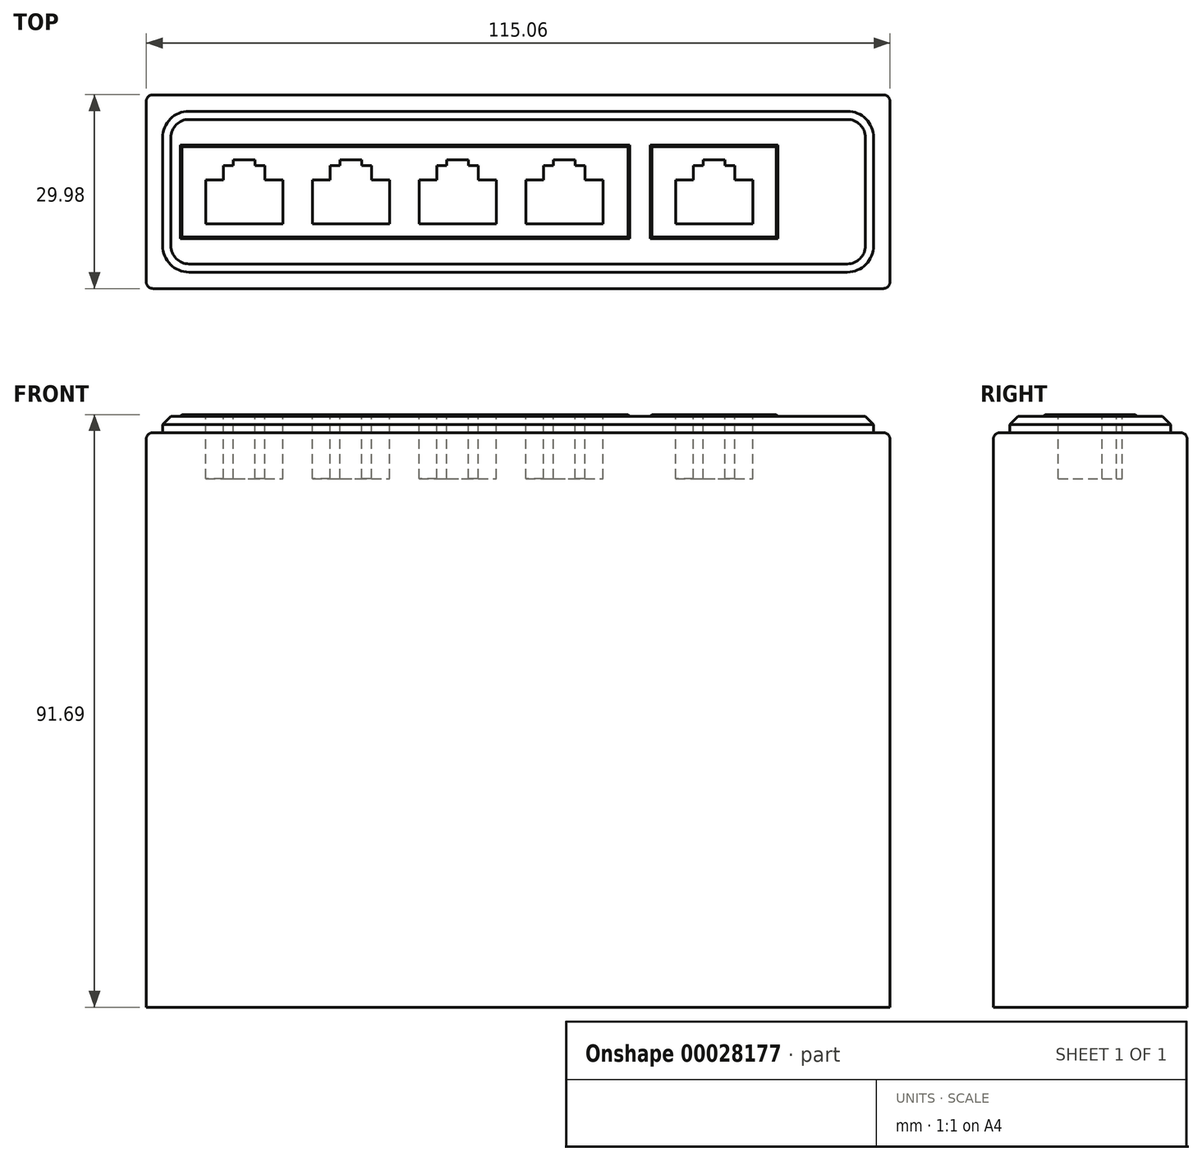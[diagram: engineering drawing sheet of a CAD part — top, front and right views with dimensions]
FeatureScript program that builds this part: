
annotation { "Feature Type Name" : "Feature", "Feature Type Description" : "" }
export const myFeature = defineFeature(function(context is Context, id is Id, definition is map)
    precondition{}
    {
        {
            var Q0;
            Q0=qCreatedBy(makeId("Front.planeOp"),FACE);
            var sketch = newSketch(context, id + "F0", { "sketchPlane" : qUnion([Q0])});
            skLineSegment(sketch, "E0.bottom", {"start": v(-57.53, -45.72) * mm, "end": v(57.53, -45.72) * mm});
            skLineSegment(sketch, "E0.top", {"start": v(-57.53, 43.18) * mm, "end": v(57.53, 43.18) * mm});
            skLineSegment(sketch, "E0.left", {"start": v(-57.53, -45.72) * mm, "end": v(-57.53, 43.18) * mm});
            skLineSegment(sketch, "E0.right", {"start": v(57.53, -45.72) * mm, "end": v(57.53, 43.18) * mm});
            skSolve(sketch);
        }
        {
            var Q0;
            Q0=qSketchRegion(id+"F0",true);
            extrude(context, id + "F1", {"entities" : qUnion([Q0]), "endBound" : BoundingType.SYMMETRIC, "depth" : 29.97 * mm});
        }
        {
            var Q0;
            Q0=makeQuery(id+"F1.opExtrude","SWEPT_FACE",FACE,{"disambiguationData":[OSD([sQuery(id+"F0.wireOp",EDGE,"E0.top")])]});
            var sketch = newSketch(context, id + "F2", { "sketchPlane" : qUnion([Q0])});
            skLineSegment(sketch, "E1.bottom", {"start": v(-50.93, 12.45) * mm, "end": v(50.93, 12.45) * mm});
            skLineSegment(sketch, "E1.top", {"start": v(-50.93, -12.45) * mm, "end": v(50.93, -12.45) * mm});
            skLineSegment(sketch, "E1.left", {"start": v(-55, 8.38) * mm, "end": v(-55, -8.38) * mm});
            skLineSegment(sketch, "E1.right", {"start": v(55, 8.38) * mm, "end": v(55, -8.38) * mm});
            skPoint(sketch, "E2.visualSharp", {"position": v(55, 12.45) * mm});
            skArc(sketch, "E2.filletArc", {"start": v(55, 8.38) * mm, "mid": v(53.8, 11.26) * mm, "end": v(50.93, 12.45) * mm});
            skPoint(sketch, "E3.visualSharp", {"position": v(55, -12.45) * mm});
            skArc(sketch, "E3.filletArc", {"start": v(50.93, -12.45) * mm, "mid": v(53.8, -11.26) * mm, "end": v(55, -8.38) * mm});
            skPoint(sketch, "E4.visualSharp", {"position": v(-55, 12.45) * mm});
            skArc(sketch, "E4.filletArc", {"start": v(-50.93, 12.45) * mm, "mid": v(-53.8, 11.26) * mm, "end": v(-55, 8.38) * mm});
            skPoint(sketch, "E5.visualSharp", {"position": v(-55, -12.45) * mm});
            skArc(sketch, "E5.filletArc", {"start": v(-55, -8.38) * mm, "mid": v(-53.8, -11.26) * mm, "end": v(-50.93, -12.45) * mm});
            skSolve(sketch);
        }
        {
            var Q0;
            Q0=qSketchRegion(id+"F2",true);
            extrude(context, id + "F3", {"entities" : qUnion([Q0]), "operationType" : NewBodyOperationType.ADD, "depth" : 2.54 * mm});
        }
        {
            var Q0;
            Q0=makeQuery(id+"F1.opExtrude","SWEPT_EDGE",EDGE,{"disambiguationData":[OSD([sQuery(id+"F0.wireOp",EDGE,"E0.top"),sQuery(id+"F0.wireOp",EDGE,"E0.right")])]});
            var Q1;
            Q1=makeQuery(id+"F1.opExtrude","CAP_EDGE",EDGE,{"disambiguationData":[OSD([sQuery(id+"F0.wireOp",EDGE,"E0.top")])],"isStart":true});
            var Q2;
            Q2=makeQuery(id+"F1.opExtrude","CAP_EDGE",EDGE,{"disambiguationData":[OSD([sQuery(id+"F0.wireOp",EDGE,"E0.top")])],"isStart":false});
            var Q3;
            Q3=makeQuery(id+"F1.opExtrude","SWEPT_EDGE",EDGE,{"disambiguationData":[OSD([sQuery(id+"F0.wireOp",EDGE,"E0.top"),sQuery(id+"F0.wireOp",EDGE,"E0.left")])]});
            var Q4;
            Q4=makeQuery(id+"F1.opExtrude","CAP_EDGE",EDGE,{"disambiguationData":[OSD([sQuery(id+"F0.wireOp",EDGE,"E0.right")])],"isStart":false});
            var Q5;
            Q5=makeQuery(id+"F1.opExtrude","CAP_EDGE",EDGE,{"disambiguationData":[OSD([sQuery(id+"F0.wireOp",EDGE,"E0.left")])],"isStart":false});
            var Q6;
            Q6=makeQuery(id+"F1.opExtrude","CAP_EDGE",EDGE,{"disambiguationData":[OSD([sQuery(id+"F0.wireOp",EDGE,"E0.left")])],"isStart":true});
            var Q7;
            Q7=makeQuery(id+"F1.opExtrude","CAP_EDGE",EDGE,{"disambiguationData":[OSD([sQuery(id+"F0.wireOp",EDGE,"E0.right")])],"isStart":true});
            fillet(context, id + "F4", {"entities" : qUnion([Q0, Q1, Q2, Q3, Q4, Q5, Q6, Q7]), "radius" : 1.02 * mm, "tangentPropagation" : true, "allowEdgeOverflow" : false});
        }
        {
            var Q0;
            Q0=makeQuery(id+"F3.opExtrude","CAP_FACE",FACE,{"disambiguationData":[OSD([sQuery(id+"F2.wireOp",EDGE,"E1.bottom"),sQuery(id+"F2.wireOp",EDGE,"E1.top"),sQuery(id+"F2.wireOp",EDGE,"E1.left"),sQuery(id+"F2.wireOp",EDGE,"E1.right"),sQuery(id+"F2.wireOp",EDGE,"E2.filletArc"),sQuery(id+"F2.wireOp",EDGE,"E3.filletArc"),sQuery(id+"F2.wireOp",EDGE,"E4.filletArc"),sQuery(id+"F2.wireOp",EDGE,"E5.filletArc")])],"isStart":false});
            var sketch = newSketch(context, id + "F5", { "sketchPlane" : qUnion([Q0])});
            skLineSegment(sketch, "E6.bottom", {"start": v(20.46, -7.24) * mm, "end": v(40.17, -7.24) * mm});
            skLineSegment(sketch, "E6.top", {"start": v(20.46, 7.24) * mm, "end": v(40.17, 7.24) * mm});
            skLineSegment(sketch, "E6.left", {"start": v(20.46, -7.24) * mm, "end": v(20.46, 7.24) * mm});
            skLineSegment(sketch, "E6.right", {"start": v(40.17, -7.24) * mm, "end": v(40.17, 7.24) * mm});
            skLineSegment(sketch, "E7.bottom", {"start": v(-52.25, -7.24) * mm, "end": v(17.29, -7.24) * mm});
            skLineSegment(sketch, "E7.top", {"start": v(-52.25, 7.24) * mm, "end": v(17.29, 7.24) * mm});
            skLineSegment(sketch, "E7.left", {"start": v(-52.25, -7.24) * mm, "end": v(-52.25, 7.24) * mm});
            skLineSegment(sketch, "E7.right", {"start": v(17.29, -7.24) * mm, "end": v(17.29, 7.24) * mm});
            skSolve(sketch);
        }
        {
            var Q0;
            Q0=qSketchRegion(id+"F5",true);
            extrude(context, id + "F6", {"entities" : qUnion([Q0]), "operationType" : NewBodyOperationType.ADD, "depth" : 0.25 * mm});
        }
        {
            var Q0;
            Q0=makeQuery(id+"F6.opExtrude","CAP_FACE",FACE,{"disambiguationData":[OSD([sQuery(id+"F5.wireOp",EDGE,"E7.bottom"),sQuery(id+"F5.wireOp",EDGE,"E7.top"),sQuery(id+"F5.wireOp",EDGE,"E7.left"),sQuery(id+"F5.wireOp",EDGE,"E7.right")])],"isStart":false});
            var sketch = newSketch(context, id + "F7", { "sketchPlane" : qUnion([Q0])});
            skLineSegment(sketch, "E8", {"start": v(-42.4, -4.95) * mm, "end": v(-42.4, 4.95) * mm, "construction": true});
            skLineSegment(sketch, "E9", {"start": v(-48.36, -4.95) * mm, "end": v(-36.42, -4.95) * mm});
            skLineSegment(sketch, "E10.MirrorCS", {"start": v(27.12, 1.83) * mm, "end": v(27.12, 4.03) * mm});
            skLineSegment(sketch, "E11", {"start": v(33.52, 1.83) * mm, "end": v(36.29, 1.83) * mm});
            skLineSegment(sketch, "E12.MirrorCS", {"start": v(-45.59, 1.83) * mm, "end": v(-45.59, 4.03) * mm});
            skLineSegment(sketch, "E13", {"start": v(-39.2, 1.83) * mm, "end": v(-36.42, 1.83) * mm});
            skLineSegment(sketch, "E14", {"start": v(24.35, -4.95) * mm, "end": v(36.29, -4.95) * mm});
            skLineSegment(sketch, "E15", {"start": v(36.29, -4.95) * mm, "end": v(36.29, 1.83) * mm});
            skLineSegment(sketch, "E16.MirrorCS", {"start": v(-45.59, 1.83) * mm, "end": v(-48.36, 1.83) * mm});
            skLineSegment(sketch, "E17.MirrorCS", {"start": v(27.12, 1.83) * mm, "end": v(24.35, 1.83) * mm});
            skLineSegment(sketch, "E18.MirrorCS", {"start": v(-48.36, -4.95) * mm, "end": v(-48.36, 1.83) * mm});
            skLineSegment(sketch, "E19", {"start": v(30.32, -4.95) * mm, "end": v(30.32, 4.95) * mm, "construction": true});
            skLineSegment(sketch, "E20", {"start": v(33.52, 1.83) * mm, "end": v(33.52, 4.03) * mm});
            skLineSegment(sketch, "E21", {"start": v(-36.42, -4.95) * mm, "end": v(-36.42, 1.83) * mm});
            skLineSegment(sketch, "E22", {"start": v(-39.2, 1.83) * mm, "end": v(-39.2, 4.03) * mm});
            skLineSegment(sketch, "E23", {"start": v(-44.09, 4.95) * mm, "end": v(-40.7, 4.95) * mm});
            skLineSegment(sketch, "E24.MirrorCS", {"start": v(24.35, -4.95) * mm, "end": v(24.35, 1.83) * mm});
            skLineSegment(sketch, "E25", {"start": v(28.62, 4.95) * mm, "end": v(32.02, 4.95) * mm});
            skLineSegment(sketch, "E26.MirrorCS", {"start": v(27.12, 4.03) * mm, "end": v(28.62, 4.03) * mm});
            skLineSegment(sketch, "E27.MirrorCS", {"start": v(-44.09, 4.03) * mm, "end": v(-44.09, 4.95) * mm});
            skLineSegment(sketch, "E28.MirrorCS", {"start": v(28.62, 4.03) * mm, "end": v(28.62, 4.95) * mm});
            skLineSegment(sketch, "E29", {"start": v(33.52, 4.03) * mm, "end": v(32.02, 4.03) * mm});
            skLineSegment(sketch, "E30", {"start": v(32.02, 4.03) * mm, "end": v(32.02, 4.95) * mm});
            skLineSegment(sketch, "E31", {"start": v(-40.7, 4.03) * mm, "end": v(-40.7, 4.95) * mm});
            skLineSegment(sketch, "E32.MirrorCS", {"start": v(-45.59, 4.03) * mm, "end": v(-44.09, 4.03) * mm});
            skLineSegment(sketch, "E33", {"start": v(-39.2, 4.03) * mm, "end": v(-40.7, 4.03) * mm});
            skLineSegment(sketch, "E34.1.0.0", {"start": v(-22.68, 1.83) * mm, "end": v(-22.68, 4.03) * mm});
            skLineSegment(sketch, "E34.1.0.1", {"start": v(-31.85, -4.95) * mm, "end": v(-31.85, 1.83) * mm});
            skLineSegment(sketch, "E34.1.0.2", {"start": v(-19.91, -4.95) * mm, "end": v(-19.91, 1.83) * mm});
            skLineSegment(sketch, "E34.1.0.3", {"start": v(-29.08, 1.83) * mm, "end": v(-29.08, 4.03) * mm});
            skLineSegment(sketch, "E34.1.0.4", {"start": v(-31.85, -4.95) * mm, "end": v(-19.91, -4.95) * mm});
            skLineSegment(sketch, "E34.1.0.5", {"start": v(-25.88, -4.95) * mm, "end": v(-25.88, 4.95) * mm, "construction": true});
            skLineSegment(sketch, "E34.1.0.6", {"start": v(-29.08, 1.83) * mm, "end": v(-31.85, 1.83) * mm});
            skLineSegment(sketch, "E34.1.0.7", {"start": v(-22.68, 1.83) * mm, "end": v(-19.91, 1.83) * mm});
            skLineSegment(sketch, "E34.1.0.8", {"start": v(-27.58, 4.95) * mm, "end": v(-24.18, 4.95) * mm});
            skLineSegment(sketch, "E34.1.0.9", {"start": v(-24.18, 4.03) * mm, "end": v(-24.18, 4.95) * mm});
            skLineSegment(sketch, "E34.1.0.10", {"start": v(-22.68, 4.03) * mm, "end": v(-24.18, 4.03) * mm});
            skLineSegment(sketch, "E34.1.0.11", {"start": v(-29.08, 4.03) * mm, "end": v(-27.58, 4.03) * mm});
            skLineSegment(sketch, "E34.1.0.12", {"start": v(-27.58, 4.03) * mm, "end": v(-27.58, 4.95) * mm});
            skLineSegment(sketch, "E34.2.0.0", {"start": v(-6.17, 1.83) * mm, "end": v(-6.17, 4.03) * mm});
            skLineSegment(sketch, "E34.2.0.1", {"start": v(-15.34, -4.95) * mm, "end": v(-15.34, 1.83) * mm});
            skLineSegment(sketch, "E34.2.0.2", {"start": v(-3.4, -4.95) * mm, "end": v(-3.4, 1.83) * mm});
            skLineSegment(sketch, "E34.2.0.3", {"start": v(-12.57, 1.83) * mm, "end": v(-12.57, 4.03) * mm});
            skLineSegment(sketch, "E34.2.0.4", {"start": v(-15.34, -4.95) * mm, "end": v(-3.4, -4.95) * mm});
            skLineSegment(sketch, "E34.2.0.5", {"start": v(-9.37, -4.95) * mm, "end": v(-9.37, 4.95) * mm, "construction": true});
            skLineSegment(sketch, "E34.2.0.6", {"start": v(-12.57, 1.83) * mm, "end": v(-15.34, 1.83) * mm});
            skLineSegment(sketch, "E34.2.0.7", {"start": v(-6.17, 1.83) * mm, "end": v(-3.4, 1.83) * mm});
            skLineSegment(sketch, "E34.2.0.8", {"start": v(-11.07, 4.95) * mm, "end": v(-7.67, 4.95) * mm});
            skLineSegment(sketch, "E34.2.0.9", {"start": v(-7.67, 4.03) * mm, "end": v(-7.67, 4.95) * mm});
            skLineSegment(sketch, "E34.2.0.10", {"start": v(-6.17, 4.03) * mm, "end": v(-7.67, 4.03) * mm});
            skLineSegment(sketch, "E34.2.0.11", {"start": v(-12.57, 4.03) * mm, "end": v(-11.07, 4.03) * mm});
            skLineSegment(sketch, "E34.2.0.12", {"start": v(-11.07, 4.03) * mm, "end": v(-11.07, 4.95) * mm});
            skLineSegment(sketch, "E34.3.0.0", {"start": v(10.34, 1.83) * mm, "end": v(10.34, 4.03) * mm});
            skLineSegment(sketch, "E34.3.0.1", {"start": v(1.17, -4.95) * mm, "end": v(1.17, 1.83) * mm});
            skLineSegment(sketch, "E34.3.0.2", {"start": v(13.1, -4.95) * mm, "end": v(13.1, 1.83) * mm});
            skLineSegment(sketch, "E34.3.0.3", {"start": v(3.94, 1.83) * mm, "end": v(3.94, 4.03) * mm});
            skLineSegment(sketch, "E34.3.0.4", {"start": v(1.17, -4.95) * mm, "end": v(13.1, -4.95) * mm});
            skLineSegment(sketch, "E34.3.0.5", {"start": v(7.14, -4.95) * mm, "end": v(7.14, 4.95) * mm, "construction": true});
            skLineSegment(sketch, "E34.3.0.6", {"start": v(3.94, 1.83) * mm, "end": v(1.17, 1.83) * mm});
            skLineSegment(sketch, "E34.3.0.7", {"start": v(10.34, 1.83) * mm, "end": v(13.1, 1.83) * mm});
            skLineSegment(sketch, "E34.3.0.8", {"start": v(5.44, 4.95) * mm, "end": v(8.84, 4.95) * mm});
            skLineSegment(sketch, "E34.3.0.9", {"start": v(8.84, 4.03) * mm, "end": v(8.84, 4.95) * mm});
            skLineSegment(sketch, "E34.3.0.10", {"start": v(10.34, 4.03) * mm, "end": v(8.84, 4.03) * mm});
            skLineSegment(sketch, "E34.3.0.11", {"start": v(3.94, 4.03) * mm, "end": v(5.44, 4.03) * mm});
            skLineSegment(sketch, "E34.3.0.12", {"start": v(5.44, 4.03) * mm, "end": v(5.44, 4.95) * mm});
            skLineSegment(sketch, "E34.direction1", {"start": v(-39.2, 1.83) * mm, "end": v(-22.68, 1.83) * mm, "construction": true});
            skSolve(sketch);
        }
        {
            var Q0;
            Q0=qSketchRegion(id+"F7",true);
            extrude(context, id + "F8", {"entities" : qUnion([Q0]), "operationType" : NewBodyOperationType.REMOVE, "oppositeDirection" : true, "depth" : 9.9 * mm});
        }
        {
            var Q0;
            Q0=makeQuery(id+"F6.opExtrude","CAP_EDGE",EDGE,{"disambiguationData":[OSD([sQuery(id+"F5.wireOp",EDGE,"E7.top")])],"isStart":false});
            var Q1;
            Q1=makeQuery(id+"F6.opExtrude","CAP_EDGE",EDGE,{"disambiguationData":[OSD([sQuery(id+"F5.wireOp",EDGE,"E7.left")])],"isStart":false});
            var Q2;
            Q2=makeQuery(id+"F6.opExtrude","CAP_EDGE",EDGE,{"disambiguationData":[OSD([sQuery(id+"F5.wireOp",EDGE,"E7.bottom")])],"isStart":false});
            var Q3;
            Q3=makeQuery(id+"F6.opExtrude","CAP_EDGE",EDGE,{"disambiguationData":[OSD([sQuery(id+"F5.wireOp",EDGE,"E7.right")])],"isStart":false});
            var Q4;
            Q4=makeQuery(id+"F6.opExtrude","CAP_EDGE",EDGE,{"disambiguationData":[OSD([sQuery(id+"F5.wireOp",EDGE,"E6.left")])],"isStart":false});
            var Q5;
            Q5=makeQuery(id+"F6.opExtrude","CAP_EDGE",EDGE,{"disambiguationData":[OSD([sQuery(id+"F5.wireOp",EDGE,"E6.bottom")])],"isStart":false});
            var Q6;
            Q6=makeQuery(id+"F6.opExtrude","CAP_EDGE",EDGE,{"disambiguationData":[OSD([sQuery(id+"F5.wireOp",EDGE,"E6.right")])],"isStart":false});
            var Q7;
            Q7=makeQuery(id+"F6.opExtrude","CAP_EDGE",EDGE,{"disambiguationData":[OSD([sQuery(id+"F5.wireOp",EDGE,"E6.top")])],"isStart":false});
            chamfer(context, id + "F9", {"entities" : qUnion([Q0, Q1, Q2, Q3, Q4, Q5, Q6, Q7]), "width" : 0.25 * mm, "tangentPropagation" : true});
        }
        {
            var Q0;
            Q0=makeQuery(id+"F3.opExtrude","CAP_EDGE",EDGE,{"disambiguationData":[OSD([sQuery(id+"F2.wireOp",EDGE,"E1.left")])],"isStart":false});
            var Q1;
            Q1=makeQuery(id+"F3.opExtrude","CAP_EDGE",EDGE,{"disambiguationData":[OSD([sQuery(id+"F2.wireOp",EDGE,"E5.filletArc")])],"isStart":false});
            var Q2;
            Q2=makeQuery(id+"F3.opExtrude","CAP_EDGE",EDGE,{"disambiguationData":[OSD([sQuery(id+"F2.wireOp",EDGE,"E1.top")])],"isStart":false});
            var Q3;
            Q3=makeQuery(id+"F3.opExtrude","CAP_EDGE",EDGE,{"disambiguationData":[OSD([sQuery(id+"F2.wireOp",EDGE,"E4.filletArc")])],"isStart":false});
            var Q4;
            Q4=makeQuery(id+"F3.opExtrude","CAP_EDGE",EDGE,{"disambiguationData":[OSD([sQuery(id+"F2.wireOp",EDGE,"E1.bottom")])],"isStart":false});
            var Q5;
            Q5=makeQuery(id+"F3.opExtrude","CAP_EDGE",EDGE,{"disambiguationData":[OSD([sQuery(id+"F2.wireOp",EDGE,"E3.filletArc")])],"isStart":false});
            var Q6;
            Q6=makeQuery(id+"F3.opExtrude","CAP_EDGE",EDGE,{"disambiguationData":[OSD([sQuery(id+"F2.wireOp",EDGE,"E1.right")])],"isStart":false});
            var Q7;
            Q7=makeQuery(id+"F3.opExtrude","CAP_EDGE",EDGE,{"disambiguationData":[OSD([sQuery(id+"F2.wireOp",EDGE,"E2.filletArc")])],"isStart":false});
            chamfer(context, id + "F10", {"entities" : qUnion([Q0, Q1, Q2, Q3, Q4, Q5, Q6, Q7]), "width" : 1.27 * mm, "tangentPropagation" : true});
        }
    });
